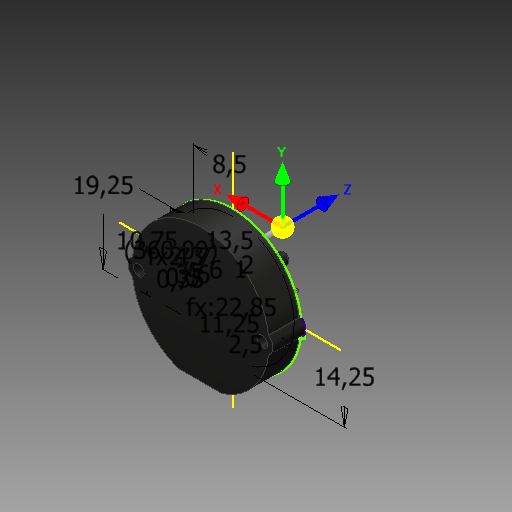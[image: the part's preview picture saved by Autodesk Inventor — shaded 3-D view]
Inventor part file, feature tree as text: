
AUTODESK INVENTOR PART (.ipt)
format: ipt  version: 2019 (Build 230136000, 136)  size: 249,344 bytes
history: native  units: mm
features: extrude x6, sketch x2, other x1, fillet x1
ambient origin geometry x8: Origin, YZ Plane, XZ Plane, XY Plane, X Axis, Y Axis, Z Axis, Center Point
bodies: Solid1 (feature_tree)
feature tree (10):
  other  "Rotational:1"
  sketch  "Sketch1"  dims[d2=2.3mm d3=4.7mm]
  extrude  "Extrusion1"  Depth=2.3mm
  sketch  "Sketch2"  dims[d4=13.5mm d5=20.0mm d7=360.0deg d9=2.0mm d10=1.0mm d11=6.0mm d12=2.5mm d13=10.75mm d14=19.25mm d16=8.5mm d17=0.35mm d18=0.5mm d19=11.25mm d20=3.6mm d21=20.0mm d23=22.85mm d24=20.0mm d26=7.7mm d29=7.0mm d30=0.0mm d31=3.0mm d32=0.0mm d33=0.5mm d34=10.95mm d35=0.0mm d36=2.3mm d37=0.0mm d38=2.8mm d39=0.0mm d40=0.3mm d41=0.0mm d42=0.0mm d43=0.0mm d44=0.0mm d45=0.0mm d48=14.25mm]
  extrude  "Extrusion2"  Depth=0.3mm TaperAngle=360.0deg
  fillet  "Fillet1"  Radius=2.0mm
  extrude  "Extrusion3"  Depth=1.0mm
  extrude  "Extrusion4"  Depth=6.0mm
  extrude  "Extrusion5"  Depth=0.3mm
  extrude  "Extrusion6"  Depth=10.75mm
